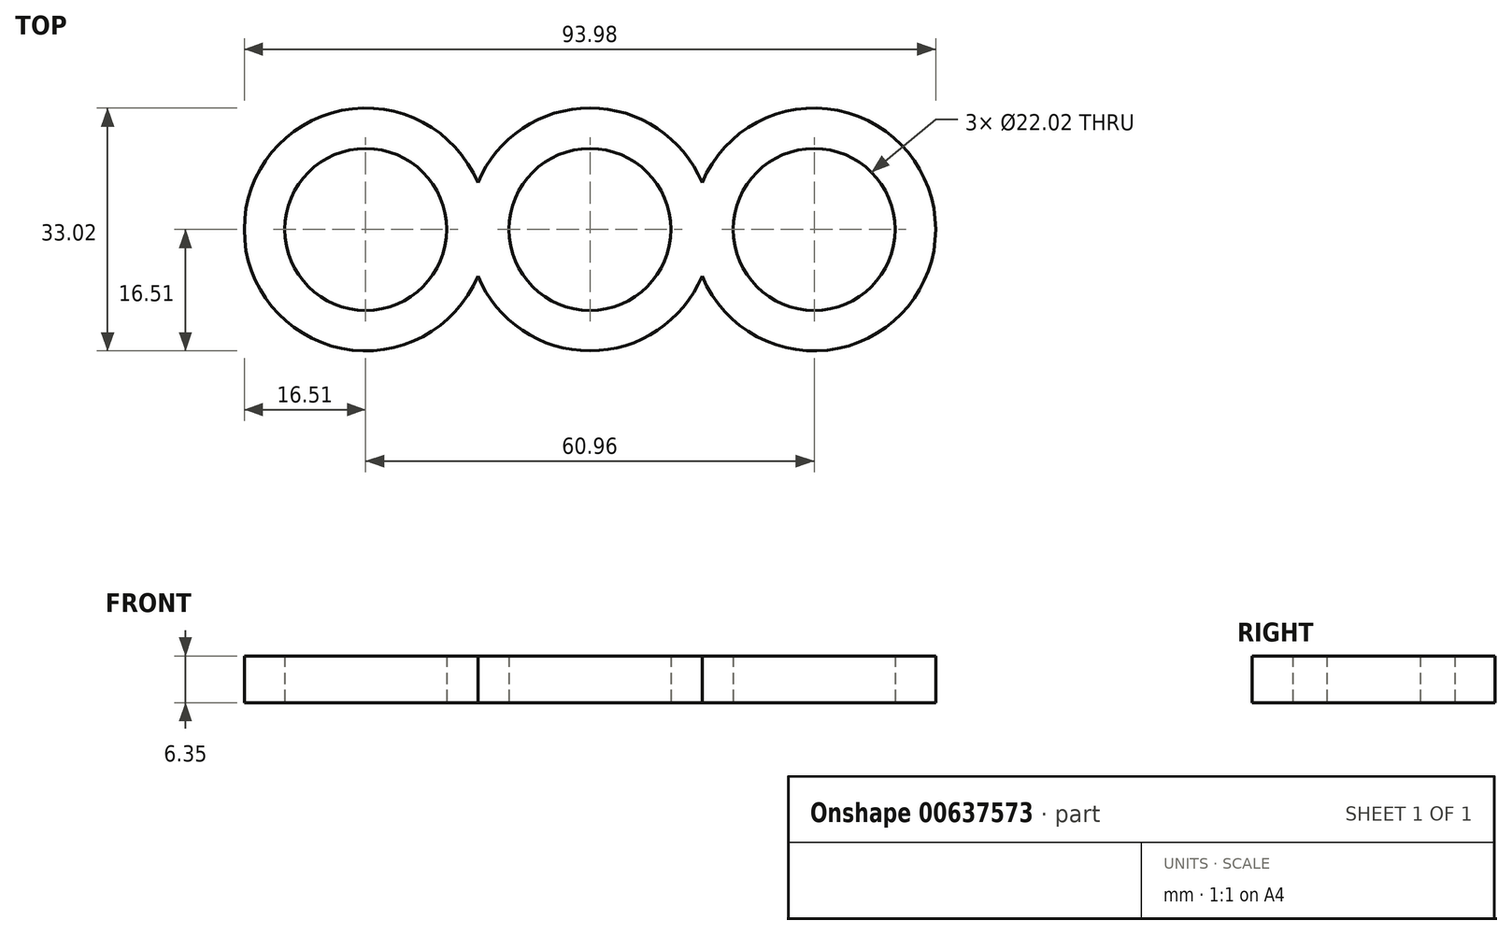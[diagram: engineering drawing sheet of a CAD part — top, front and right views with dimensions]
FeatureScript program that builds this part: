
annotation { "Feature Type Name" : "Feature", "Feature Type Description" : "" }
export const myFeature = defineFeature(function(context is Context, id is Id, definition is map)
    precondition{}
    {
        {
            var Q0;
            Q0=qCreatedBy(makeId("Top.planeOp"),FACE);
            var sketch = newSketch(context, id + "F0", { "sketchPlane" : qUnion([Q0])});
            skCircle(sketch, "E0", {"center": v(0, 0) * mm, "radius": 11.01 * mm});
            skLineSegment(sketch, "E1", {"start": v(0, 0) * mm, "end": v(-30.48, 0) * mm});
            skLineSegment(sketch, "E2", {"start": v(0, 0) * mm, "end": v(30.48, 0) * mm});
            skCircle(sketch, "E3", {"center": v(-30.48, 0) * mm, "radius": 11.01 * mm});
            skCircle(sketch, "E4", {"center": v(30.48, 0) * mm, "radius": 11.01 * mm});
            skCircle(sketch, "E5", {"center": v(-30.48, 0) * mm, "radius": 16.51 * mm});
            skCircle(sketch, "E6", {"center": v(0, 0) * mm, "radius": 16.51 * mm});
            skCircle(sketch, "E7", {"center": v(30.48, 0) * mm, "radius": 16.51 * mm});
            skSolve(sketch);
        }
        {
            var Q0;
            Q0 = qSketchRegion(id + "F0", true);
            extrude(context, id + "F1", {"entities" : qUnion([Q0]), "depth" : 6.35 * mm, "offsetDistance" : 25.4 * mm});
        }
        {
            var Q0;
            Q0 = qSketchRegion(id + "F0", true);
            extrude(context, id + "F2", {"entities" : qUnion([Q0]), "operationType" : NewBodyOperationType.ADD, "depth" : 6.35 * mm, "offsetDistance" : 25.4 * mm});
        }
    });
